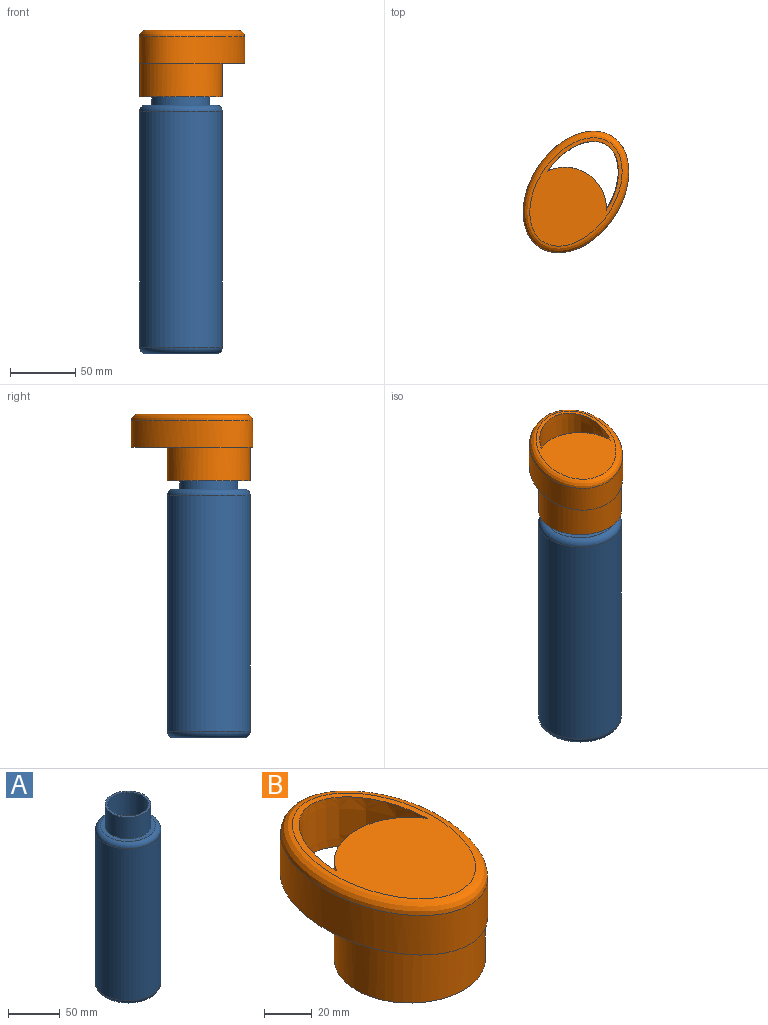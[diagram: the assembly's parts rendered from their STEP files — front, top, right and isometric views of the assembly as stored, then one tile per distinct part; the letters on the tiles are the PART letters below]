
ASSEMBLY  parts=2 mates=1
PART A: 11 faces, bbox 68.7x68.7x215.9 mm
  f0: cylinder r=31.75mm len=180.34mm, axis (0,0,-1), area 35976.2mm2, adj f9,f10
  f1: plane 53.34x53.34mm, normal (0,0,1), area 682.8mm2, adj f3,f9
  f2: plane 53.34x53.34mm, normal (0,0,-1), area 2234.6mm2, adj f10
  f3: cylinder r=22.23mm len=44.45mm, axis (0,0,-1), area 3547mm2, adj f1,f4
  f4: plane 44.45x44.45mm, normal (0,0,1), area 334.4mm2, adj f3,f8
  f5: cylinder r=29.21mm len=185.42mm, axis (0,0,-1), area 34030.5mm2, adj f6,f7
  f6: plane 58.42x58.42mm, normal (0,0,-1), area 1463.1mm2, adj f5,f8
  f7: plane 58.42x58.42mm, normal (0,0,1), area 2680.5mm2, adj f5
  f8: cylinder r=19.69mm len=39.37mm, axis (0,0,-1), area 3455.7mm2, adj f4,f6
  f9: torus R=26.67mm, axis (0,0,1), area 1499.3mm2, adj f0,f1
  f10: torus R=26.67mm, axis (0,0,1), area 1499.3mm2, adj f0,f2
PART B: 10 faces, bbox 69.9x101.6x50.8 mm
  f0: cylinder r=31.75mm len=63.5mm, axis (0,0,-1), area 6710.7mm2, adj f1,f2,f3,f4,f6
  f1: plane 63.5x63.5mm, normal (0,0,-1), area 1579.5mm2, adj f0,f8
  f2: plane 79.94x69.85mm, normal (0,0,-1), area 1106mm2, adj f0,f4,f5
  f3: plane 57.21x21.66mm, normal (0,0,-1), area 132.2mm2, adj f0,f5
  f4: extruded ~54.08x41.65mm, area 2755.5mm2, adj f0,f2,f6
  f5: extruded ~101.57x69.83mm, area 5519.5mm2, adj f2,f3,f7
  f6: plane 91.45x59.71mm, normal (0,0,1), area 3106.9mm2, adj f0,f4,f7
  f7: bspline ~101.61x69.89mm, area 2075.2mm2, adj f5,f6
  f8: cylinder r=22.48mm len=44.96mm, axis (0,0,-1), area 3587.5mm2, adj f1,f9
  f9: plane 44.96x44.96mm, normal (0,0,-1), area 1587.5mm2, adj f8
PLACE A t=(-34.21,33.21,-28.51)mm fixed
PLACE B rot(axis=(0,0,-1),33.4deg) t=(-34.21,33.21,-22.02)mm
MATE cylindrical B.f0 <-> A.f0  axis (0,0,-1) through (-34.21,33.21,168.48)mm
